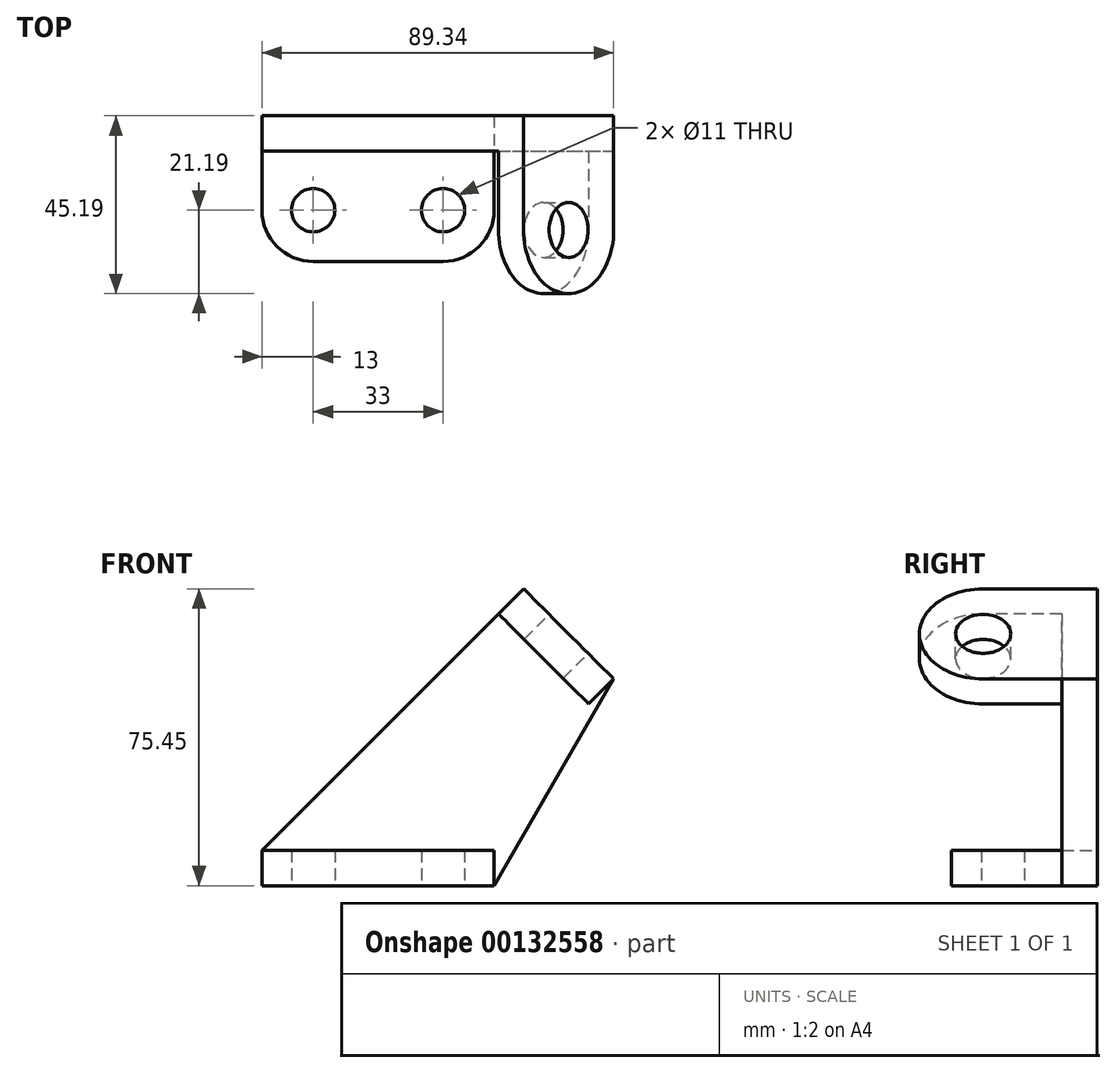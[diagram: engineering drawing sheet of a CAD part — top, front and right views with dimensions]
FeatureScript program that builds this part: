
annotation { "Feature Type Name" : "Feature", "Feature Type Description" : "" }
export const myFeature = defineFeature(function(context is Context, id is Id, definition is map)
    precondition{}
    {
        {
            var Q0;
            Q0=qCreatedBy(makeId("Top.planeOp"),FACE);
            var sketch = newSketch(context, id + "F0", { "sketchPlane" : qUnion([Q0])});
            skLineSegment(sketch, "E0", {"start": v(0, 0) * mm, "end": v(33, 0) * mm});
            skArc(sketch, "E1", {"start": v(-13, 13) * mm, "mid": v(-9.2, 3.8) * mm, "end": v(0, 0) * mm});
            skArc(sketch, "E2", {"start": v(33, 0) * mm, "mid": v(42.2, 3.8) * mm, "end": v(46, 13) * mm});
            skLineSegment(sketch, "E3", {"start": v(-13, 13) * mm, "end": v(-13, 37) * mm});
            skLineSegment(sketch, "E4", {"start": v(-13, 37) * mm, "end": v(46, 37) * mm});
            skLineSegment(sketch, "E5", {"start": v(46, 37) * mm, "end": v(46, 13) * mm});
            skCircle(sketch, "E6", {"center": v(0, 13) * mm, "radius": 5.5 * mm});
            skCircle(sketch, "E7", {"center": v(33, 13) * mm, "radius": 5.5 * mm});
            skSolve(sketch);
        }
        {
            var Q0;
            Q0=makeQuery(id+"F0.imprint","IMPRINT",FACE,{"disambiguationData":[TD([[makeQuery(id+"F0.imprint","IMPRINT",EDGE,{"derivedFrom":sQuery(id+"F0.wireOp",EDGE,"E0")}),1.0]])]});
            extrude(context, id + "F1", {"entities" : qUnion([Q0]), "depth" : 9 * mm});
        }
        {
            var Q0;
            Q0=makeQuery(id+"F1.opExtrude","SWEPT_FACE",FACE,{"disambiguationData":[OSD([sQuery(id+"F0.wireOp",EDGE,"E4")])]});
            var sketch = newSketch(context, id + "F2", { "sketchPlane" : qUnion([Q0])});
            skLineSegment(sketch, "E8", {"start": v(-46, 0) * mm, "end": v(-76.34, 52.55) * mm});
            skLineSegment(sketch, "E9", {"start": v(13, 9) * mm, "end": v(-53.45, 75.45) * mm});
            skLineSegment(sketch, "E10", {"start": v(-53.45, 75.45) * mm, "end": v(-76.34, 52.55) * mm});
            skLineSegment(sketch, "E11", {"start": v(-64.9, 64) * mm, "end": v(-109.42, 64) * mm, "construction": true});
            skLineSegment(sketch, "E12", {"start": v(-46, 0) * mm, "end": v(-101.75, 0) * mm, "construction": true});
            skSolve(sketch);
        }
        {
            var Q0;
            Q0=makeQuery(id+"F2.imprint","IMPRINT",FACE,{"disambiguationData":[TD([[makeQuery(id+"F2.imprint","IMPRINT",EDGE,{"derivedFrom":sQuery(id+"F2.wireOp",EDGE,"E8")}),-1.0]])]});
            extrude(context, id + "F3", {"entities" : qUnion([Q0]), "operationType" : NewBodyOperationType.ADD, "oppositeDirection" : true, "depth" : 9 * mm});
        }
        {
            var Q0;
            Q0=makeQuery(id+"F3.opExtrude","SWEPT_FACE",FACE,{"disambiguationData":[OSD([sQuery(id+"F2.wireOp",EDGE,"E10")])]});
            var sketch = newSketch(context, id + "F4", { "sketchPlane" : qUnion([Q0])});
            skLineSegment(sketch, "E13", {"start": v(37, 15.56) * mm, "end": v(8, 15.56) * mm});
            skPoint(sketch, "E13.endSnap0", {"position": v(32.5, 15.56) * mm});
            skLineSegment(sketch, "E14", {"start": v(37, -16.82) * mm, "end": v(8, -16.82) * mm});
            skArc(sketch, "E15", {"start": v(8, 15.56) * mm, "mid": v(-8.19, -0.63) * mm, "end": v(8, -16.82) * mm});
            skCircle(sketch, "E16", {"center": v(8, -0.63) * mm, "radius": 7 * mm});
            skSolve(sketch);
        }
        {
            var Q0;
            {var subQ0=sQuery(id+"F4.wireOp",EDGE,"E15");Q0=makeQuery(id+"F4.imprint","IMPRINT",FACE,{"disambiguationData":[TD([[makeQuery(id+"F4.imprint","IMPRINT",EDGE,{"derivedFrom":subQ0}),1.0]])]});}
            extrude(context, id + "F5", {"entities" : qUnion([Q0]), "operationType" : NewBodyOperationType.ADD, "oppositeDirection" : true, "depth" : 9 * mm});
        }
    });
